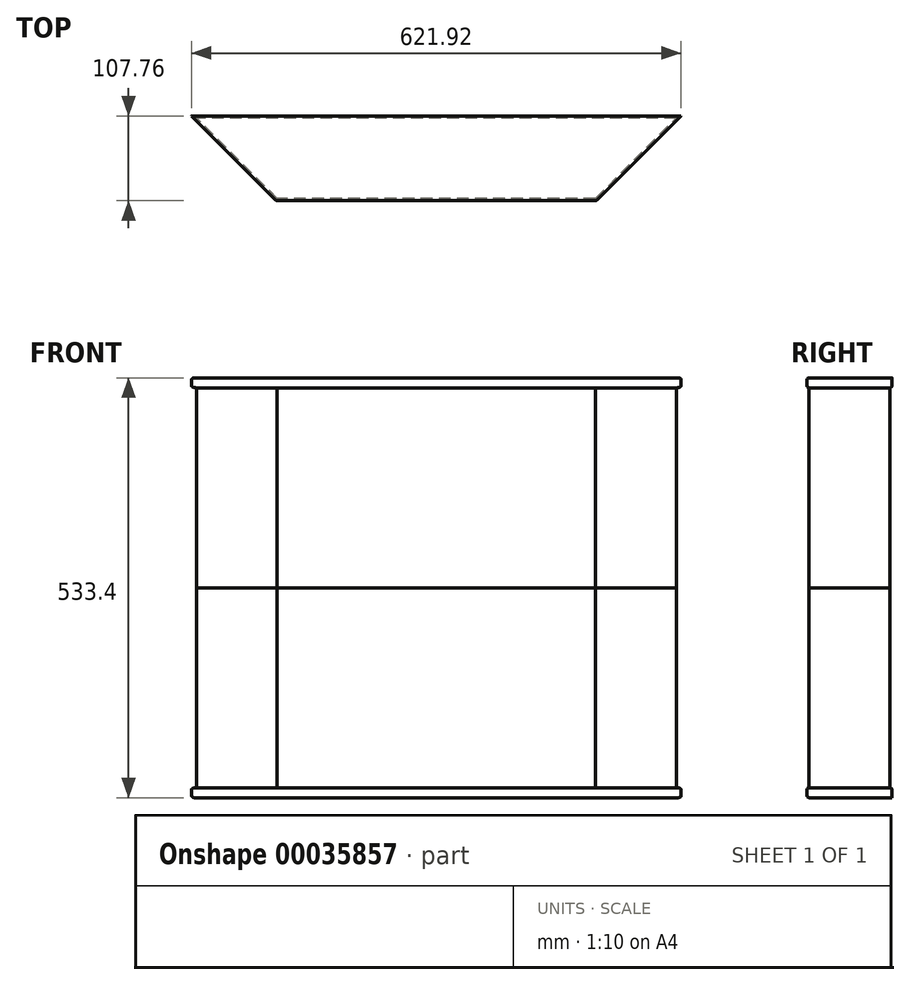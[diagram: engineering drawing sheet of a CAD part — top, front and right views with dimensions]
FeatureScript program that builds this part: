
annotation { "Feature Type Name" : "Feature", "Feature Type Description" : "" }
export const myFeature = defineFeature(function(context is Context, id is Id, definition is map)
    precondition{}
    {
        {
            var Q0;
            Q0=qCreatedBy(makeId("Top.planeOp"),FACE);
            var sketch = newSketch(context, id + "F0", { "sketchPlane" : qUnion([Q0])});
            skLineSegment(sketch, "E0", {"start": v(0, 0) * mm, "end": v(0, 0) * mm});
            skLineSegment(sketch, "E1", {"start": v(0, 0) * mm, "end": v(0, 153.31) * mm, "construction": true});
            skLineSegment(sketch, "E2", {"start": v(0, 0) * mm, "end": v(203.2, 0) * mm});
            skLineSegment(sketch, "E3", {"start": v(203.2, 0) * mm, "end": v(203.2, 0) * mm});
            skLineSegment(sketch, "E4", {"start": v(203.2, 0) * mm, "end": v(310.96, 107.76) * mm});
            skLineSegment(sketch, "E5", {"start": v(310.96, 107.76) * mm, "end": v(0, 107.76) * mm});
            skLineSegment(sketch, "E6.MirrorCS", {"start": v(-310.96, 107.76) * mm, "end": v(0, 107.76) * mm});
            skLineSegment(sketch, "E7.MirrorCS", {"start": v(0, 0) * mm, "end": v(-203.2, 0) * mm});
            skLineSegment(sketch, "E8.MirrorCS", {"start": v(-203.2, 0) * mm, "end": v(-310.96, 107.76) * mm});
            skSolve(sketch);
        }
        {
            var Q0;
            Q0=makeQuery(id+"F0.imprint","IMPRINT",FACE,{"disambiguationData":[TD([[makeQuery(id+"F0.imprint","IMPRINT",EDGE,{"derivedFrom":sQuery(id+"F0.wireOp",EDGE,"E2")}),1.0]])]});
            extrude(context, id + "F1", {"entities" : qUnion([Q0]), "depth" : 12.7 * mm, "offsetDistance" : 25.4 * mm});
        }
        {
            var Q0;
            Q0=makeQuery(id+"F1.opExtrude","CAP_FACE",FACE,{"disambiguationData":[OSD([sQuery(id+"F0.wireOp",EDGE,"E2"),sQuery(id+"F0.wireOp",EDGE,"E4"),sQuery(id+"F0.wireOp",EDGE,"E5"),sQuery(id+"F0.wireOp",EDGE,"E6.MirrorCS"),sQuery(id+"F0.wireOp",EDGE,"E7.MirrorCS"),sQuery(id+"F0.wireOp",EDGE,"E8.MirrorCS")])],"isStart":false});
            var Q1;
            Q1=makeQuery(id+"F1.opExtrude","SWEPT_FACE",FACE,{"disambiguationData":[OSD([sQuery(id+"F0.wireOp",EDGE,"E2"),sQuery(id+"F0.wireOp",EDGE,"E7.MirrorCS")])]});
            var Q2;
            Q2=makeQuery(id+"F1.opExtrude","CAP_EDGE",EDGE,{"disambiguationData":[OSD([sQuery(id+"F0.wireOp",EDGE,"E4")])],"isStart":true});
            var Q3;
            Q3=makeQuery(id+"F1.opExtrude","CAP_EDGE",EDGE,{"disambiguationData":[OSD([sQuery(id+"F0.wireOp",EDGE,"E8.MirrorCS")])],"isStart":true});
            fillet(context, id + "F2", {"entities" : qUnion([Q0, Q1, Q2, Q3]), "radius" : 2.54 * mm, "tangentPropagation" : true, "allowEdgeOverflow" : false});
        }
        {
            var Q0;
            Q0=makeQuery(id+"F1.opExtrude","CAP_FACE",FACE,{"disambiguationData":[OSD([sQuery(id+"F0.wireOp",EDGE,"E2"),sQuery(id+"F0.wireOp",EDGE,"E4"),sQuery(id+"F0.wireOp",EDGE,"E5"),sQuery(id+"F0.wireOp",EDGE,"E6.MirrorCS"),sQuery(id+"F0.wireOp",EDGE,"E7.MirrorCS"),sQuery(id+"F0.wireOp",EDGE,"E8.MirrorCS")])],"isStart":false});
            extrude(context, id + "F3", {"entities" : qUnion([Q0]), "depth" : 254 * mm, "offsetDistance" : 25.4 * mm});
        }
        {
            var Q0;
            Q0=makeQuery(id+"F1.opExtrude","SWEPT_BODY",BODY,{"disambiguationData":[OSD([sQuery(id+"F0.wireOp",EDGE,"E2"),sQuery(id+"F0.wireOp",EDGE,"E4"),sQuery(id+"F0.wireOp",EDGE,"E5"),sQuery(id+"F0.wireOp",EDGE,"E6.MirrorCS"),sQuery(id+"F0.wireOp",EDGE,"E7.MirrorCS"),sQuery(id+"F0.wireOp",EDGE,"E8.MirrorCS")])]});
            var Q1;
            Q1=makeQuery(id+"F3.opExtrude","SWEPT_BODY",BODY,{"disambiguationData":[OSD([sQuery(id+"F0.wireOp",EDGE,"E2"),sQuery(id+"F0.wireOp",EDGE,"E4"),sQuery(id+"F0.wireOp",EDGE,"E5"),sQuery(id+"F0.wireOp",EDGE,"E6.MirrorCS"),sQuery(id+"F0.wireOp",EDGE,"E7.MirrorCS"),sQuery(id+"F0.wireOp",EDGE,"E8.MirrorCS")])]});
            var Q2;
            Q2=makeQuery(id+"F3.opExtrude","CAP_FACE",FACE,{"disambiguationData":[OSD([sQuery(id+"F0.wireOp",EDGE,"E2"),sQuery(id+"F0.wireOp",EDGE,"E4"),sQuery(id+"F0.wireOp",EDGE,"E5"),sQuery(id+"F0.wireOp",EDGE,"E6.MirrorCS"),sQuery(id+"F0.wireOp",EDGE,"E7.MirrorCS"),sQuery(id+"F0.wireOp",EDGE,"E8.MirrorCS")])],"isStart":false});
            mirror(context, id + "F4", {"entities" : qUnion([Q0, Q1]), "mirrorPlane" : qUnion([Q2])});
        }
    });
